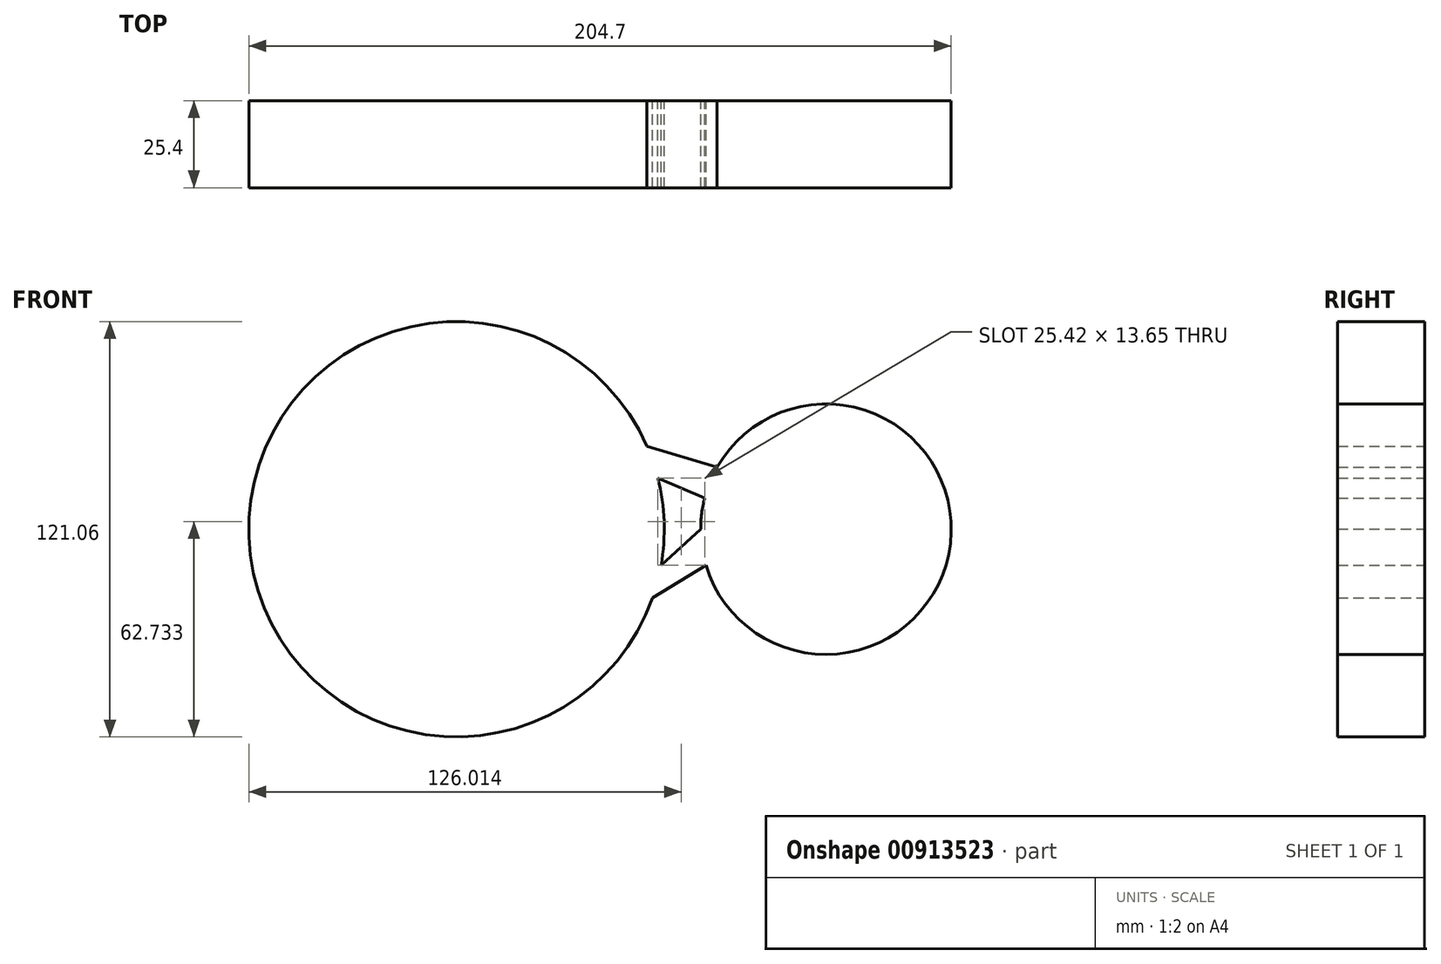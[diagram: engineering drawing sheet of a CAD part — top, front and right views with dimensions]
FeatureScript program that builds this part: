
annotation { "Feature Type Name" : "Feature", "Feature Type Description" : "" }
export const myFeature = defineFeature(function(context is Context, id is Id, definition is map)
    precondition{}
    {
        {
            var Q0;
            Q0=qCreatedBy(makeId("Front.planeOp"),FACE);
            var sketch = newSketch(context, id + "F0", { "sketchPlane" : qUnion([Q0])});
            skCircle(sketch, "E0", {"center": v(0, 0) * mm, "radius": 60.53 * mm});
            skCircle(sketch, "E1", {"center": v(107.66, 0) * mm, "radius": 36.5 * mm});
            skLineSegment(sketch, "E2", {"start": v(55.5, 24.13) * mm, "end": v(75.92, 18.04) * mm});
            skLineSegment(sketch, "E3", {"start": v(58.66, 14.91) * mm, "end": v(72.3, 9.11) * mm});
            skLineSegment(sketch, "E4", {"start": v(59.6, -10.5) * mm, "end": v(71.15, 0) * mm});
            skLineSegment(sketch, "E5", {"start": v(71.15, 0) * mm, "end": v(59.6, -10.5) * mm});
            skLineSegment(sketch, "E6", {"start": v(57.13, -19.99) * mm, "end": v(72.7, -10.5) * mm});
            skSolve(sketch);
        }
        {
            var Q0;
            Q0 = qSketchRegion(id + "F0", true);
            extrude(context, id + "F1", {"entities" : qUnion([Q0]), "depth" : 25.4 * mm, "offsetDistance" : 25.4 * mm});
        }
    });
